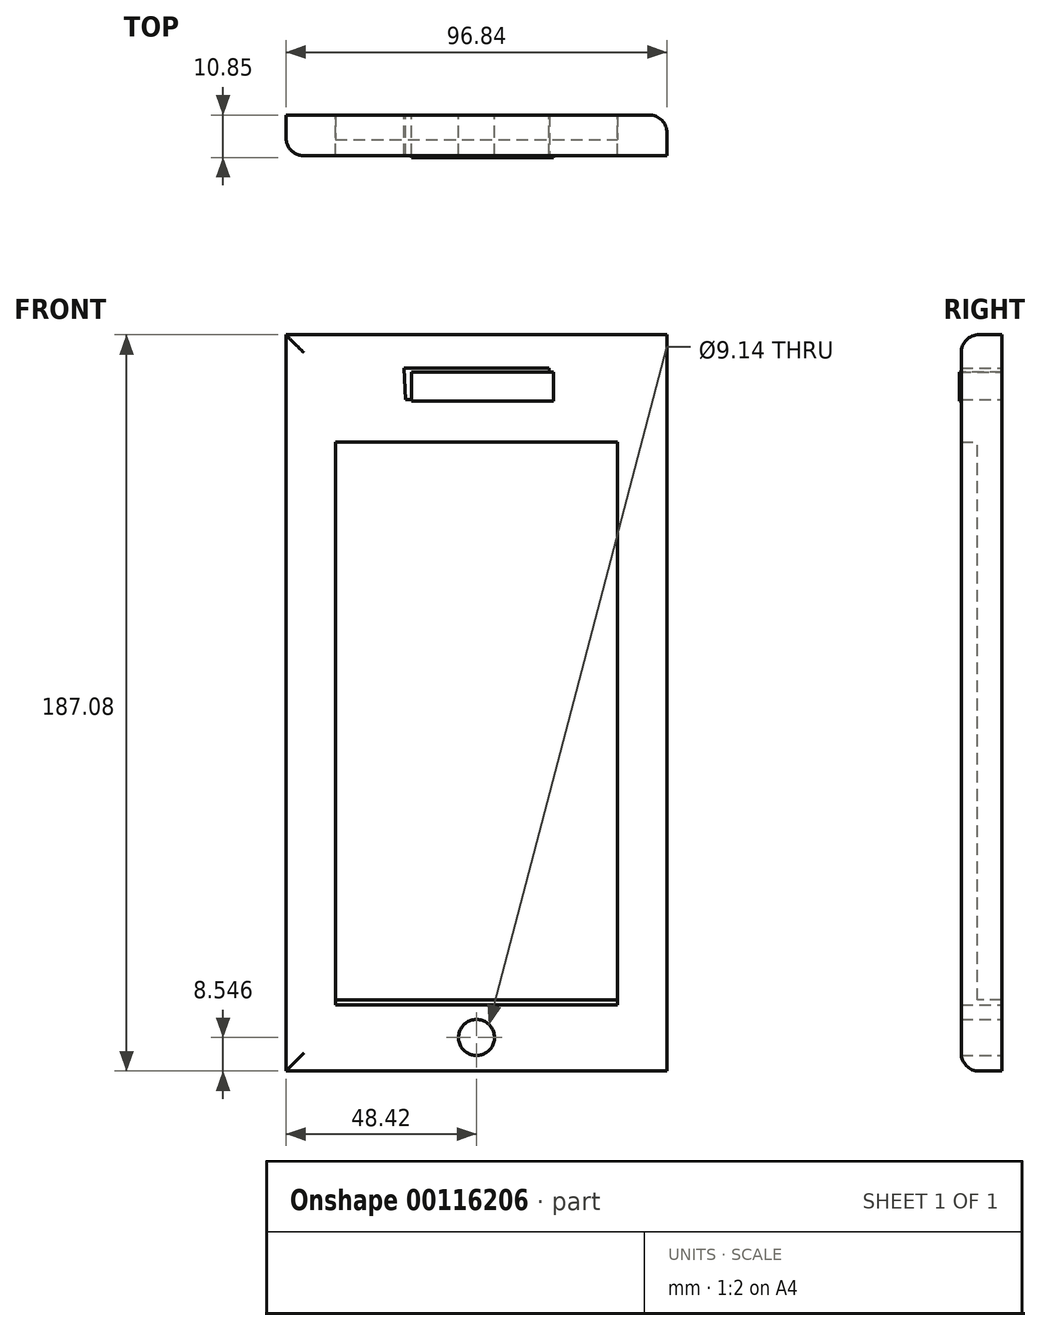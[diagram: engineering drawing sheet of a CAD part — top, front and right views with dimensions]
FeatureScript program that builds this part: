
annotation { "Feature Type Name" : "Feature", "Feature Type Description" : "" }
export const myFeature = defineFeature(function(context is Context, id is Id, definition is map)
    precondition{}
    {
        {
            var Q0;
            Q0=qCreatedBy(makeId("Front.planeOp"),FACE);
            var sketch = newSketch(context, id + "F0", { "sketchPlane" : qUnion([Q0])});
            skLineSegment(sketch, "E0.bottom", {"start": v(48.42, -93.54) * mm, "end": v(-48.42, -93.54) * mm});
            skLineSegment(sketch, "E0.top", {"start": v(48.42, 93.54) * mm, "end": v(-48.42, 93.54) * mm});
            skLineSegment(sketch, "E0.left", {"start": v(48.42, -93.54) * mm, "end": v(48.42, 93.54) * mm});
            skLineSegment(sketch, "E0.right", {"start": v(-48.42, -93.54) * mm, "end": v(-48.42, 93.54) * mm});
            skPoint(sketch, "E0.middle", {"position": v(0, 0) * mm});
            skLineSegment(sketch, "E1.bottom", {"start": v(35.86, -76.67) * mm, "end": v(-35.86, -76.67) * mm});
            skLineSegment(sketch, "E1.left", {"start": v(35.86, -76.67) * mm, "end": v(35.86, 66.32) * mm});
            skLineSegment(sketch, "E1.right", {"start": v(-35.86, -76.67) * mm, "end": v(-35.86, 66.32) * mm});
            skPoint(sketch, "E2.orphan", {"position": v(-35.86, 76.67) * mm});
            skPoint(sketch, "E3.orphan", {"position": v(35.86, 76.67) * mm});
            skLineSegment(sketch, "E4", {"start": v(-35.86, 66.32) * mm, "end": v(35.86, 66.32) * mm});
            skLineSegment(sketch, "E5.trimOffspring", {"start": v(35.86, 76.67) * mm, "end": v(35.86, 78.43) * mm});
            skCircle(sketch, "E6", {"center": v(0, -85) * mm, "radius": 4.57 * mm});
            skPoint(sketch, "E6.centerSnap0", {"position": v(0, -93.54) * mm});
            skLineSegment(sketch, "E7.bottom", {"start": v(18.48, 66.32) * mm, "end": v(-18.48, 66.32) * mm});
            skLineSegment(sketch, "E7.top", {"start": v(18.48, 85.04) * mm, "end": v(-18.48, 85.04) * mm});
            skPoint(sketch, "E7.middle", {"position": v(0, 75.68) * mm});
            skPoint(sketch, "E7.middle.positionSnap0", {"position": v(0, 66.32) * mm});
            skPoint(sketch, "E7.centerSnap0", {"position": v(0, 66.32) * mm});
            skLineSegment(sketch, "E8", {"start": v(-18.08, 77.02) * mm, "end": v(18.88, 77.02) * mm});
            skLineSegment(sketch, "E9", {"start": v(-18.48, 85.04) * mm, "end": v(-18.08, 77.02) * mm});
            skLineSegment(sketch, "E10", {"start": v(18.48, 85.04) * mm, "end": v(18.88, 77.02) * mm});
            skLineSegment(sketch, "E11", {"start": v(18.88, 77.02) * mm, "end": v(18.48, 85.04) * mm});
            skSolve(sketch);
        }
        {
            var Q0;
            Q0=makeQuery(id+"F0.imprint","IMPRINT",FACE,{"disambiguationData":[TD([[makeQuery(id+"F0.imprint","IMPRINT",EDGE,{"derivedFrom":sQuery(id+"F0.wireOp",EDGE,"E0.bottom")}),-1.0]])]});
            extrude(context, id + "F1", {"entities" : qUnion([Q0]), "depth" : 0.01 * yard});
        }
        {
            var Q0;
            Q0=makeQuery(id+"F1.opExtrude","CAP_EDGE",EDGE,{"disambiguationData":[OSD([sQuery(id+"F0.wireOp",EDGE,"E0.left")])],"isStart":true});
            var Q1;
            Q1=makeQuery(id+"F1.opExtrude","CAP_EDGE",EDGE,{"disambiguationData":[OSD([sQuery(id+"F0.wireOp",EDGE,"E0.bottom")])],"isStart":false});
            var Q2;
            Q2=makeQuery(id+"F1.opExtrude","CAP_EDGE",EDGE,{"disambiguationData":[OSD([sQuery(id+"F0.wireOp",EDGE,"E0.top")])],"isStart":false});
            var Q3;
            Q3=makeQuery(id+"F1.opExtrude","CAP_EDGE",EDGE,{"disambiguationData":[OSD([sQuery(id+"F0.wireOp",EDGE,"E0.right")])],"isStart":false});
            fillet(context, id + "F2", {"entities" : qUnion([Q0, Q1, Q2, Q3]), "radius" : 0 * yard, "tangentPropagation" : true, "allowEdgeOverflow" : false});
        }
        {
            var Q0;
            Q0=qCreatedBy(makeId("Front.planeOp"),FACE);
            var sketch = newSketch(context, id + "F3", { "sketchPlane" : qUnion([Q0])});
            skLineSegment(sketch, "E12.bottom", {"start": v(36.74, -75.47) * mm, "end": v(-36.74, -75.47) * mm});
            skLineSegment(sketch, "E12.top", {"start": v(36.74, 75.47) * mm, "end": v(-36.74, 75.47) * mm});
            skLineSegment(sketch, "E12.left", {"start": v(36.74, -75.47) * mm, "end": v(36.74, 75.47) * mm});
            skLineSegment(sketch, "E12.right", {"start": v(-36.74, -75.47) * mm, "end": v(-36.74, 75.47) * mm});
            skPoint(sketch, "E12.middle", {"position": v(0, 0) * mm});
            skSolve(sketch);
        }
        {
            var Q0;
            Q0 = qSketchRegion(id + "F3", true);
            extrude(context, id + "F4", {"entities" : qUnion([Q0]), "operationType" : NewBodyOperationType.ADD, "depth" : 6.27 * mm});
        }
        {
            var Q0;
            Q0=qCreatedBy(makeId("Front.planeOp"),FACE);
            var sketch = newSketch(context, id + "F5", { "sketchPlane" : qUnion([Q0])});
            skLineSegment(sketch, "E13.bottom", {"start": v(-16.5, 84.06) * mm, "end": v(19.6, 84.06) * mm});
            skLineSegment(sketch, "E13.top", {"start": v(-16.5, 76.7) * mm, "end": v(19.6, 76.7) * mm});
            skLineSegment(sketch, "E13.left", {"start": v(-16.5, 84.06) * mm, "end": v(-16.5, 76.7) * mm});
            skLineSegment(sketch, "E13.right", {"start": v(19.6, 84.06) * mm, "end": v(19.6, 76.7) * mm});
            skSolve(sketch);
        }
        {
            var Q0;
            Q0 = qSketchRegion(id + "F5", true);
            extrude(context, id + "F6", {"entities" : qUnion([Q0]), "operationType" : NewBodyOperationType.ADD, "depth" : 0.01 * yard});
        }
    });
